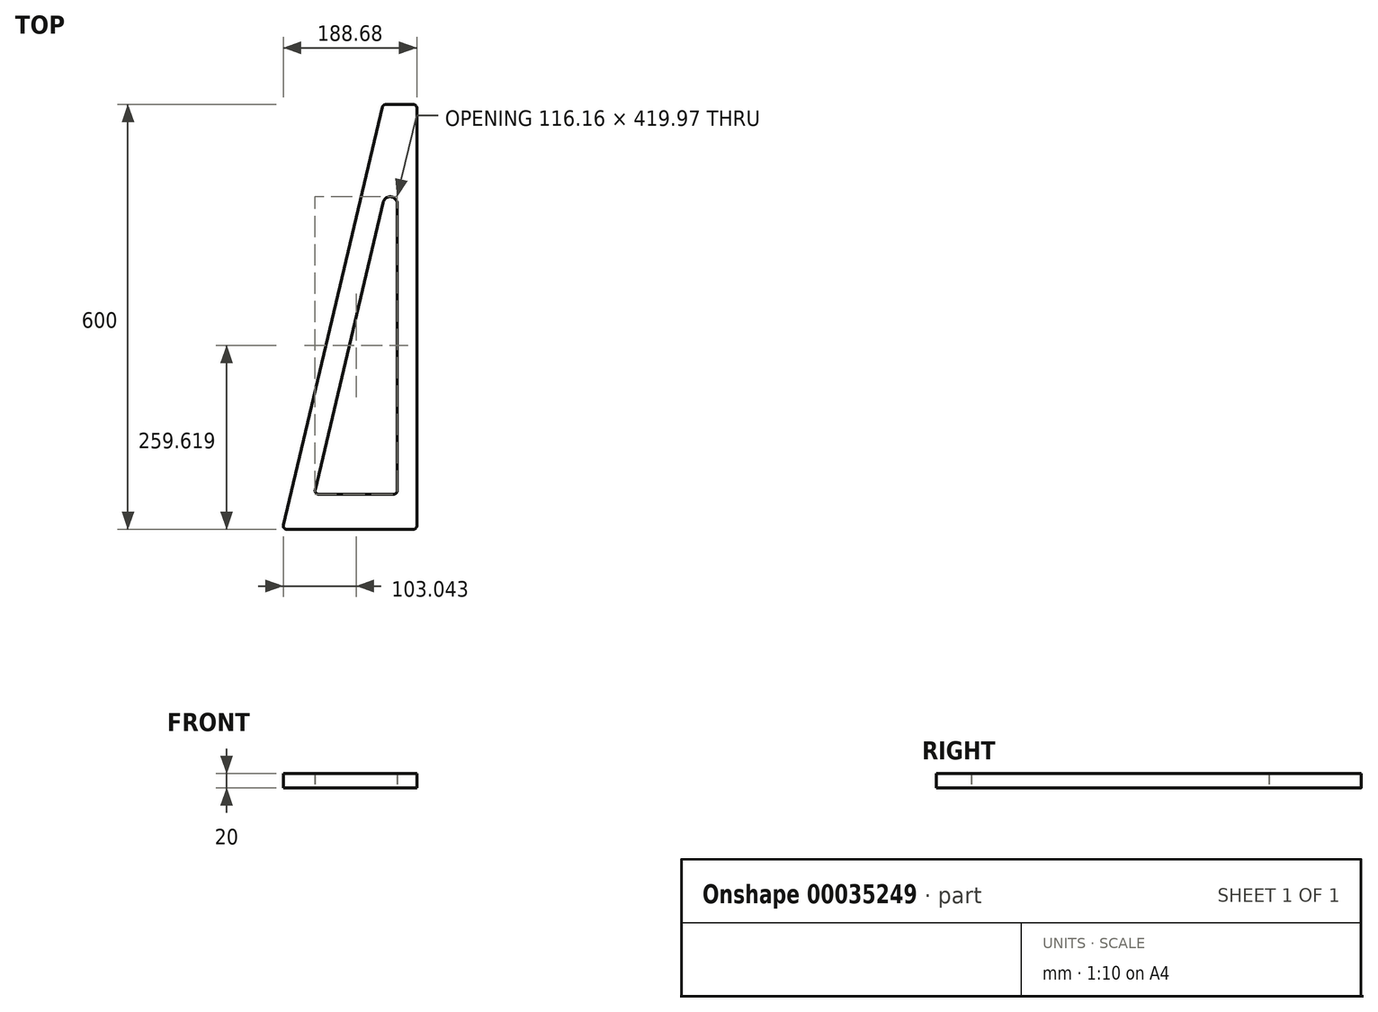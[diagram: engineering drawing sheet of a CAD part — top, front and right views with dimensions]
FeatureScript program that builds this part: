
annotation { "Feature Type Name" : "Feature", "Feature Type Description" : "" }
export const myFeature = defineFeature(function(context is Context, id is Id, definition is map)
    precondition{}
    {
        {
            var Q0;
            Q0=qCreatedBy(makeId("Top.planeOp"),FACE);
            var sketch = newSketch(context, id + "F0", { "sketchPlane" : qUnion([Q0])});
            skLineSegment(sketch, "E0.rect.bottom", {"start": v(47.23, 300) * mm, "end": v(95, 300) * mm});
            skLineSegment(sketch, "E0.rect.top", {"start": v(-95, -300) * mm, "end": v(95, -300) * mm});
            skLineSegment(sketch, "E0.rect.right", {"start": v(95, 300) * mm, "end": v(95, -300) * mm});
            skPoint(sketch, "E0.rect.middle", {"position": v(0, 0) * mm});
            skLineSegment(sketch, "E1", {"start": v(97.23, 300) * mm, "end": v(47.23, 300) * mm});
            skLineSegment(sketch, "E2", {"start": v(47.23, 300) * mm, "end": v(-95, -300) * mm});
            skPoint(sketch, "E3.orphan", {"position": v(-95, 300) * mm});
            skPoint(sketch, "E4", {"position": v(47.23, 300) * mm});
            skLineSegment(sketch, "E5", {"start": v(-50.04, -250.37) * mm, "end": v(67.44, -250.37) * mm});
            skLineSegment(sketch, "E6", {"start": v(67.44, -250.37) * mm, "end": v(67.44, 245.21) * mm});
            skLineSegment(sketch, "E7", {"start": v(-50.04, -250.37) * mm, "end": v(67.44, 245.21) * mm});
            skPoint(sketch, "E8.top.end.orphan", {"position": v(-179.43, 0) * mm});
            skSolve(sketch);
        }
        {
            var Q0;
            Q0=makeQuery(id+"F0.imprint","IMPRINT",FACE,{"disambiguationData":[TD([[makeQuery(id+"F0.imprint","IMPRINT",EDGE,{"derivedFrom":sQuery(id+"F0.wireOp",EDGE,"E0.rect.top")}),1.0]])]});
            extrude(context, id + "F1", {"entities" : qUnion([Q0]), "depth" : 20 * mm});
        }
        {
            var Q0;
            Q0=makeQuery(id+"F1.opExtrude","SWEPT_EDGE",EDGE,{"disambiguationData":[OSD([sQuery(id+"F0.wireOp",EDGE,"E0.rect.right"),sQuery(id+"F0.wireOp",EDGE,"E1")])]});
            var Q1;
            Q1=makeQuery(id+"F1.opExtrude","SWEPT_EDGE",EDGE,{"disambiguationData":[OSD([sQuery(id+"F0.wireOp",EDGE,"E0.rect.top"),sQuery(id+"F0.wireOp",EDGE,"E0.rect.right")])]});
            var Q2;
            Q2=makeQuery(id+"F1.opExtrude","SWEPT_EDGE",EDGE,{"disambiguationData":[OSD([sQuery(id+"F0.wireOp",EDGE,"E0.rect.top"),sQuery(id+"F0.wireOp",EDGE,"E2")])]});
            var Q3;
            Q3=makeQuery(id+"F1.opExtrude","SWEPT_EDGE",EDGE,{"disambiguationData":[OSD([sQuery(id+"F0.wireOp",EDGE,"E5"),sQuery(id+"F0.wireOp",EDGE,"E6")])]});
            var Q4;
            Q4=makeQuery(id+"F1.opExtrude","SWEPT_EDGE",EDGE,{"disambiguationData":[OSD([sQuery(id+"F0.wireOp",EDGE,"E5"),sQuery(id+"F0.wireOp",EDGE,"E7")])]});
            var Q5;
            Q5=makeQuery(id+"F1.opExtrude","SWEPT_EDGE",EDGE,{"disambiguationData":[OSD([sQuery(id+"F0.wireOp",EDGE,"E1"),sQuery(id+"F0.wireOp",EDGE,"E2")])]});
            fillet(context, id + "F2", {"entities" : qUnion([Q0, Q1, Q2, Q3, Q4, Q5]), "radius" : 5 * mm, "tangentPropagation" : true, "allowEdgeOverflow" : false});
        }
        {
            var Q0;
            Q0=makeQuery(id+"F1.opExtrude","SWEPT_EDGE",EDGE,{"disambiguationData":[OSD([sQuery(id+"F0.wireOp",EDGE,"E6"),sQuery(id+"F0.wireOp",EDGE,"E7")])]});
            fillet(context, id + "F3", {"entities" : qUnion([Q0]), "radius" : 10 * mm, "tangentPropagation" : true, "allowEdgeOverflow" : false});
        }
    });
